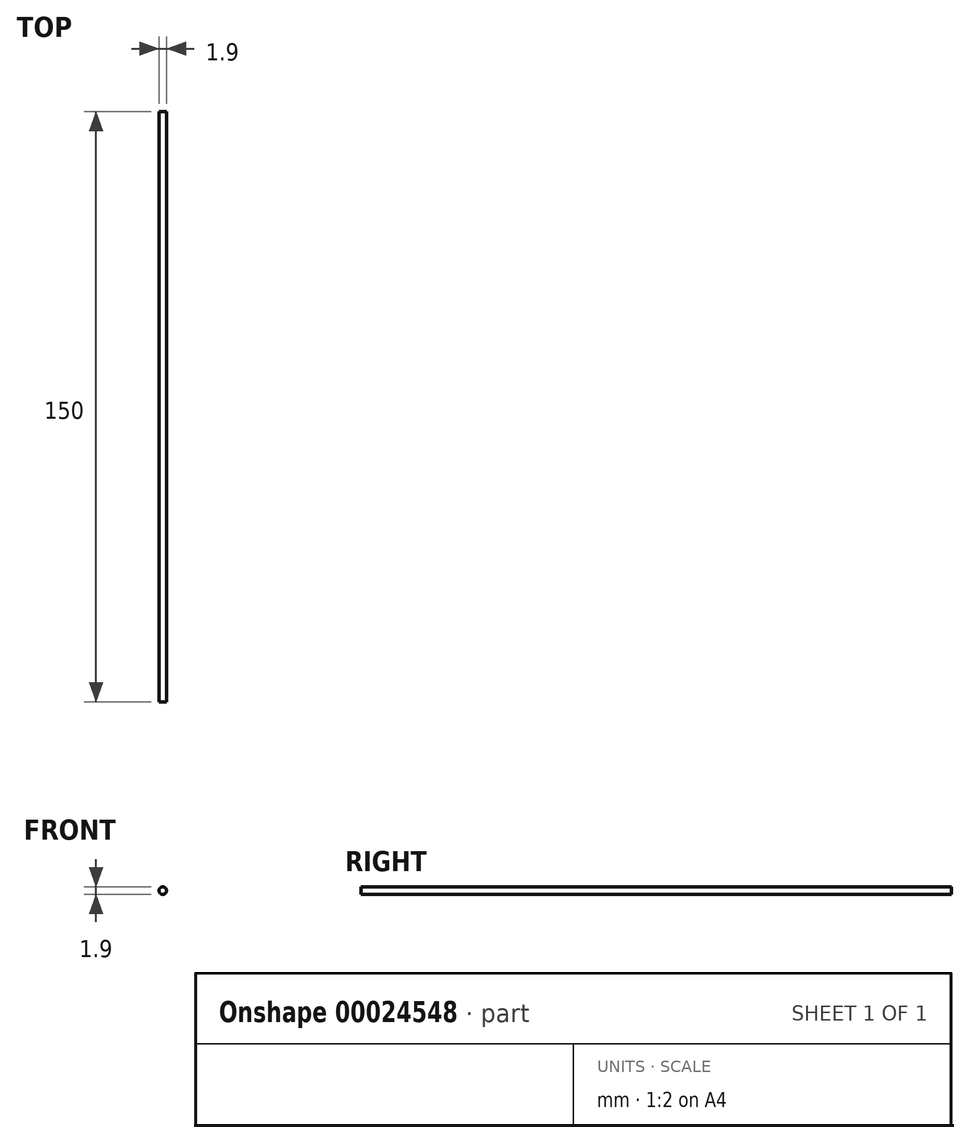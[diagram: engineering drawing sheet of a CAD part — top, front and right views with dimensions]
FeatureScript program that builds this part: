
annotation { "Feature Type Name" : "Feature", "Feature Type Description" : "" }
export const myFeature = defineFeature(function(context is Context, id is Id, definition is map)
    precondition{}
    {
        {
            var Q0;
            Q0=qCreatedBy(makeId("Front.planeOp"),FACE);
            var sketch = newSketch(context, id + "F0", { "sketchPlane" : qUnion([Q0])});
            skCircle(sketch, "E0", {"center": v(0, 0) * mm, "radius": 0.95 * mm});
            skSolve(sketch);
        }
        {
            var Q0;
            Q0=makeQuery(id+"F0.imprint","IMPRINT",FACE,{"disambiguationData":[TD([[makeQuery(id+"F0.imprint","IMPRINT",EDGE,{"derivedFrom":sQuery(id+"F0.wireOp",EDGE,"E0")}),1.0]])]});
            extrude(context, id + "F1", {"entities" : qUnion([Q0]), "depth" : 150 * mm});
        }
    });
